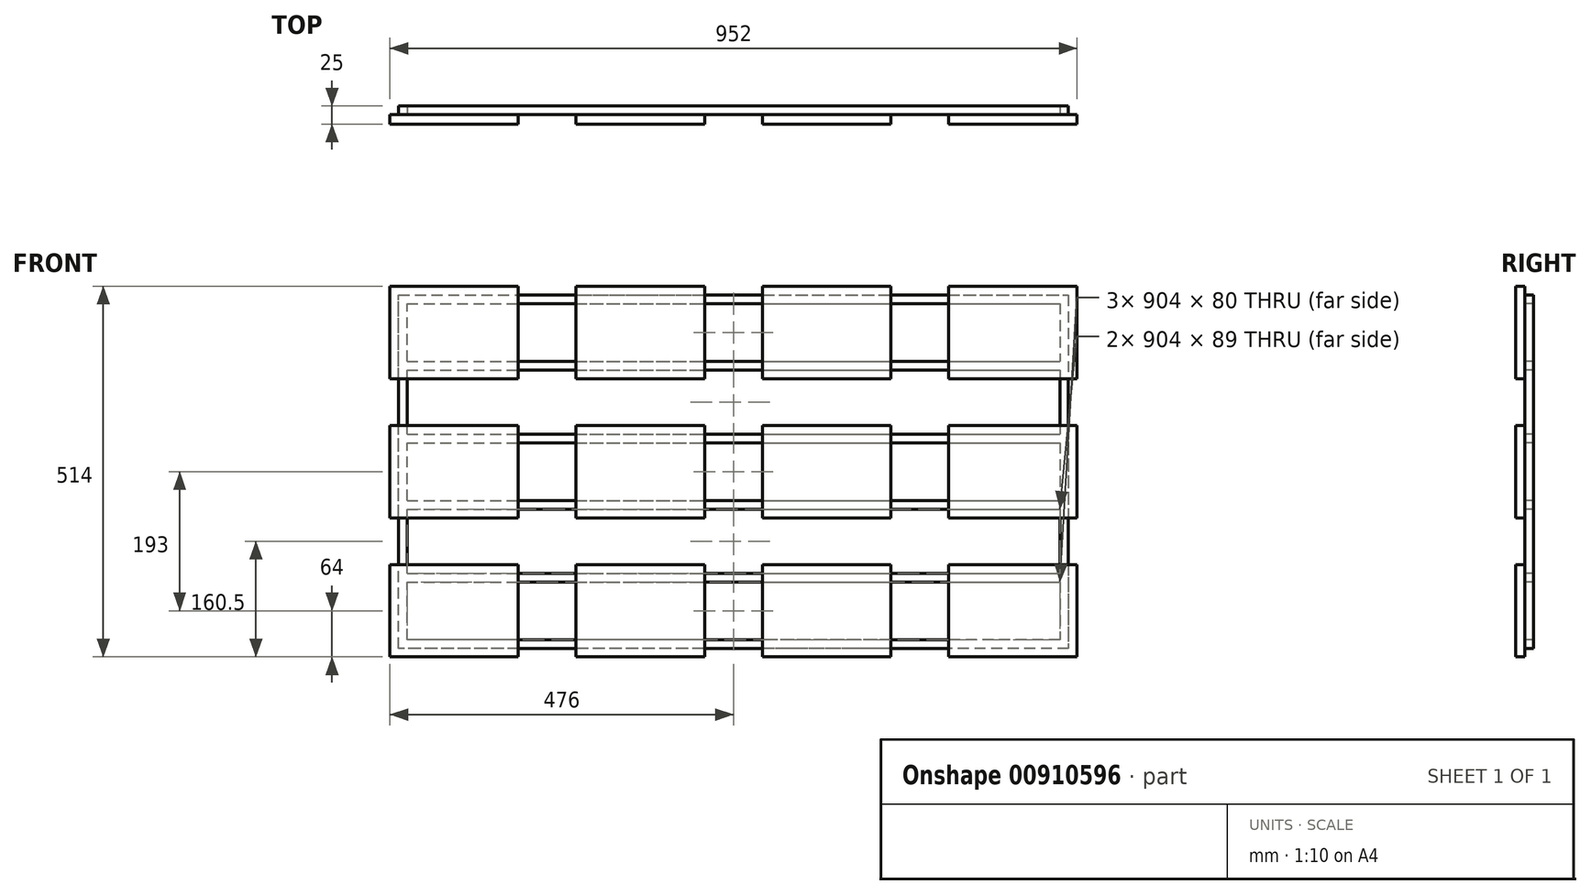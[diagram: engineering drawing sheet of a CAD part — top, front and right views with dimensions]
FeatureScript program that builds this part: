
annotation { "Feature Type Name" : "Feature", "Feature Type Description" : "" }
export const myFeature = defineFeature(function(context is Context, id is Id, definition is map)
    precondition{}
    {
        {
            var Q0;
            Q0=qCreatedBy(makeId("Front.planeOp"),FACE);
            var sketch = newSketch(context, id + "F0", { "sketchPlane" : qUnion([Q0])});
            skLineSegment(sketch, "E0", {"start": v(0, 0) * mm, "end": v(952, 0) * mm, "construction": true});
            skLineSegment(sketch, "E1", {"start": v(952, 0) * mm, "end": v(952, -514) * mm, "construction": true});
            skLineSegment(sketch, "E2", {"start": v(952, -514) * mm, "end": v(0, -514) * mm, "construction": true});
            skLineSegment(sketch, "E3", {"start": v(0, -514) * mm, "end": v(0, 0) * mm, "construction": true});
            skLineSegment(sketch, "E4.0", {"start": v(24, -24) * mm, "end": v(928, -24) * mm});
            skLineSegment(sketch, "E4.1", {"start": v(24, -490) * mm, "end": v(24, -410) * mm});
            skLineSegment(sketch, "E4.2", {"start": v(928, -490) * mm, "end": v(24, -490) * mm});
            skLineSegment(sketch, "E4.3", {"start": v(928, -24) * mm, "end": v(928, -104) * mm});
            skLineSegment(sketch, "E5", {"start": v(24, -116) * mm, "end": v(928, -116) * mm});
            skLineSegment(sketch, "E6", {"start": v(24, -205) * mm, "end": v(928, -205) * mm});
            skLineSegment(sketch, "E7", {"start": v(24, -309) * mm, "end": v(928, -309) * mm});
            skLineSegment(sketch, "E8", {"start": v(24, -398) * mm, "end": v(928, -398) * mm});
            skLineSegment(sketch, "E9.0", {"start": v(24, -104) * mm, "end": v(928, -104) * mm});
            skLineSegment(sketch, "E10.0", {"start": v(24, -217) * mm, "end": v(928, -217) * mm});
            skLineSegment(sketch, "E11.0", {"start": v(24, -410) * mm, "end": v(928, -410) * mm});
            skLineSegment(sketch, "E12.0", {"start": v(24, -297) * mm, "end": v(928, -297) * mm});
            skLineSegment(sketch, "E13.trimOffspring", {"start": v(928, -116) * mm, "end": v(928, -205) * mm});
            skLineSegment(sketch, "E14.trimOffspring", {"start": v(928, -217) * mm, "end": v(928, -297) * mm});
            skLineSegment(sketch, "E15.trimOffspring", {"start": v(928, -309) * mm, "end": v(928, -398) * mm});
            skLineSegment(sketch, "E16.trimOffspring", {"start": v(928, -410) * mm, "end": v(928, -490) * mm});
            skLineSegment(sketch, "E17.trimOffspring", {"start": v(24, -104) * mm, "end": v(24, -24) * mm});
            skLineSegment(sketch, "E18.trimOffspring", {"start": v(24, -205) * mm, "end": v(24, -116) * mm});
            skLineSegment(sketch, "E19.trimOffspring", {"start": v(24, -398) * mm, "end": v(24, -309) * mm});
            skLineSegment(sketch, "E20.trimOffspring", {"start": v(24, -297) * mm, "end": v(24, -217) * mm});
            skLineSegment(sketch, "E21.0", {"start": v(12, -502) * mm, "end": v(12, -12) * mm});
            skLineSegment(sketch, "E21.1", {"start": v(940, -502) * mm, "end": v(12, -502) * mm});
            skLineSegment(sketch, "E21.2", {"start": v(940, -12) * mm, "end": v(940, -502) * mm});
            skLineSegment(sketch, "E21.3", {"start": v(12, -12) * mm, "end": v(940, -12) * mm});
            skSolve(sketch);
        }
        {
            var Q0;
            Q0=makeQuery(id+"F0.imprint","IMPRINT",FACE,{"disambiguationData":[TD([[makeQuery(id+"F0.imprint","IMPRINT",EDGE,{"derivedFrom":sQuery(id+"F0.wireOp",EDGE,"E4.0")}),1.0]])]});
            extrude(context, id + "F1", {"entities" : qUnion([Q0]), "oppositeDirection" : true, "depth" : 12 * mm, "offsetDistance" : 25 * mm});
        }
        {
            var Q0;
            Q0=qCreatedBy(makeId("Front.planeOp"),FACE);
            var sketch = newSketch(context, id + "F2", { "sketchPlane" : qUnion([Q0])});
            skLineSegment(sketch, "E22.bottom", {"start": v(0, 0) * mm, "end": v(178, 0) * mm});
            skLineSegment(sketch, "E22.top", {"start": v(0, -128) * mm, "end": v(178, -128) * mm});
            skLineSegment(sketch, "E22.left", {"start": v(0, 0) * mm, "end": v(0, -128) * mm});
            skLineSegment(sketch, "E22.right", {"start": v(178, 0) * mm, "end": v(178, -128) * mm});
            skLineSegment(sketch, "E23.bottom", {"start": v(258, 0) * mm, "end": v(436, 0) * mm});
            skLineSegment(sketch, "E23.top", {"start": v(258, -128) * mm, "end": v(436, -128) * mm});
            skLineSegment(sketch, "E23.left", {"start": v(258, 0) * mm, "end": v(258, -128) * mm});
            skLineSegment(sketch, "E23.right", {"start": v(436, 0) * mm, "end": v(436, -128) * mm});
            skLineSegment(sketch, "E24.bottom", {"start": v(516, 0) * mm, "end": v(694, 0) * mm});
            skLineSegment(sketch, "E24.top", {"start": v(516, -128) * mm, "end": v(694, -128) * mm});
            skLineSegment(sketch, "E24.left", {"start": v(516, 0) * mm, "end": v(516, -128) * mm});
            skLineSegment(sketch, "E24.right", {"start": v(694, 0) * mm, "end": v(694, -128) * mm});
            skLineSegment(sketch, "E25.bottom", {"start": v(774, 0) * mm, "end": v(952, 0) * mm});
            skLineSegment(sketch, "E25.top", {"start": v(774, -128) * mm, "end": v(952, -128) * mm});
            skLineSegment(sketch, "E25.left", {"start": v(774, 0) * mm, "end": v(774, -128) * mm});
            skLineSegment(sketch, "E25.right", {"start": v(952, 0) * mm, "end": v(952, -128) * mm});
            skLineSegment(sketch, "E26.bottom", {"start": v(0, -193) * mm, "end": v(178, -193) * mm});
            skLineSegment(sketch, "E26.top", {"start": v(0, -321) * mm, "end": v(178, -321) * mm});
            skLineSegment(sketch, "E26.left", {"start": v(0, -193) * mm, "end": v(0, -321) * mm});
            skLineSegment(sketch, "E26.right", {"start": v(178, -193) * mm, "end": v(178, -321) * mm});
            skLineSegment(sketch, "E27.bottom", {"start": v(258, -193) * mm, "end": v(436, -193) * mm});
            skLineSegment(sketch, "E27.top", {"start": v(258, -321) * mm, "end": v(436, -321) * mm});
            skLineSegment(sketch, "E27.left", {"start": v(258, -193) * mm, "end": v(258, -321) * mm});
            skLineSegment(sketch, "E27.right", {"start": v(436, -193) * mm, "end": v(436, -321) * mm});
            skLineSegment(sketch, "E28.bottom", {"start": v(516, -193) * mm, "end": v(694, -193) * mm});
            skLineSegment(sketch, "E28.top", {"start": v(516, -321) * mm, "end": v(694, -321) * mm});
            skLineSegment(sketch, "E28.left", {"start": v(516, -193) * mm, "end": v(516, -321) * mm});
            skLineSegment(sketch, "E28.right", {"start": v(694, -193) * mm, "end": v(694, -321) * mm});
            skLineSegment(sketch, "E29.bottom", {"start": v(774, -193) * mm, "end": v(952, -193) * mm});
            skLineSegment(sketch, "E29.top", {"start": v(774, -321) * mm, "end": v(952, -321) * mm});
            skLineSegment(sketch, "E29.left", {"start": v(774, -193) * mm, "end": v(774, -321) * mm});
            skLineSegment(sketch, "E29.right", {"start": v(952, -193) * mm, "end": v(952, -321) * mm});
            skLineSegment(sketch, "E30.bottom", {"start": v(0, -386) * mm, "end": v(178, -386) * mm});
            skLineSegment(sketch, "E30.top", {"start": v(0, -514) * mm, "end": v(178, -514) * mm});
            skLineSegment(sketch, "E30.left", {"start": v(0, -386) * mm, "end": v(0, -514) * mm});
            skLineSegment(sketch, "E30.right", {"start": v(178, -386) * mm, "end": v(178, -514) * mm});
            skLineSegment(sketch, "E31.bottom", {"start": v(258, -386) * mm, "end": v(436, -386) * mm});
            skLineSegment(sketch, "E31.top", {"start": v(258, -514) * mm, "end": v(436, -514) * mm});
            skLineSegment(sketch, "E31.left", {"start": v(258, -386) * mm, "end": v(258, -514) * mm});
            skLineSegment(sketch, "E31.right", {"start": v(436, -386) * mm, "end": v(436, -514) * mm});
            skLineSegment(sketch, "E32.bottom", {"start": v(516, -386) * mm, "end": v(694, -386) * mm});
            skLineSegment(sketch, "E32.top", {"start": v(516, -514) * mm, "end": v(694, -514) * mm});
            skLineSegment(sketch, "E32.left", {"start": v(516, -386) * mm, "end": v(516, -514) * mm});
            skLineSegment(sketch, "E32.right", {"start": v(694, -386) * mm, "end": v(694, -514) * mm});
            skLineSegment(sketch, "E33.bottom", {"start": v(774, -386) * mm, "end": v(952, -386) * mm});
            skLineSegment(sketch, "E33.top", {"start": v(774, -514) * mm, "end": v(952, -514) * mm});
            skLineSegment(sketch, "E33.left", {"start": v(774, -386) * mm, "end": v(774, -514) * mm});
            skLineSegment(sketch, "E33.right", {"start": v(952, -386) * mm, "end": v(952, -514) * mm});
            skLineSegment(sketch, "E34", {"start": v(178, 0) * mm, "end": v(258, 0) * mm, "construction": true});
            skLineSegment(sketch, "E35", {"start": v(436, 0) * mm, "end": v(516, 0) * mm, "construction": true});
            skLineSegment(sketch, "E36", {"start": v(694, 0) * mm, "end": v(774, 0) * mm, "construction": true});
            skLineSegment(sketch, "E37", {"start": v(0, -128) * mm, "end": v(0, -193) * mm, "construction": true});
            skLineSegment(sketch, "E38", {"start": v(0, -321) * mm, "end": v(0, -386) * mm, "construction": true});
            skSolve(sketch);
        }
        {
            var Q0;
            Q0 = qSketchRegion(id + "F2", true);
            extrude(context, id + "F3", {"entities" : qUnion([Q0]), "depth" : 13 * mm, "offsetDistance" : 25 * mm});
        }
    });
